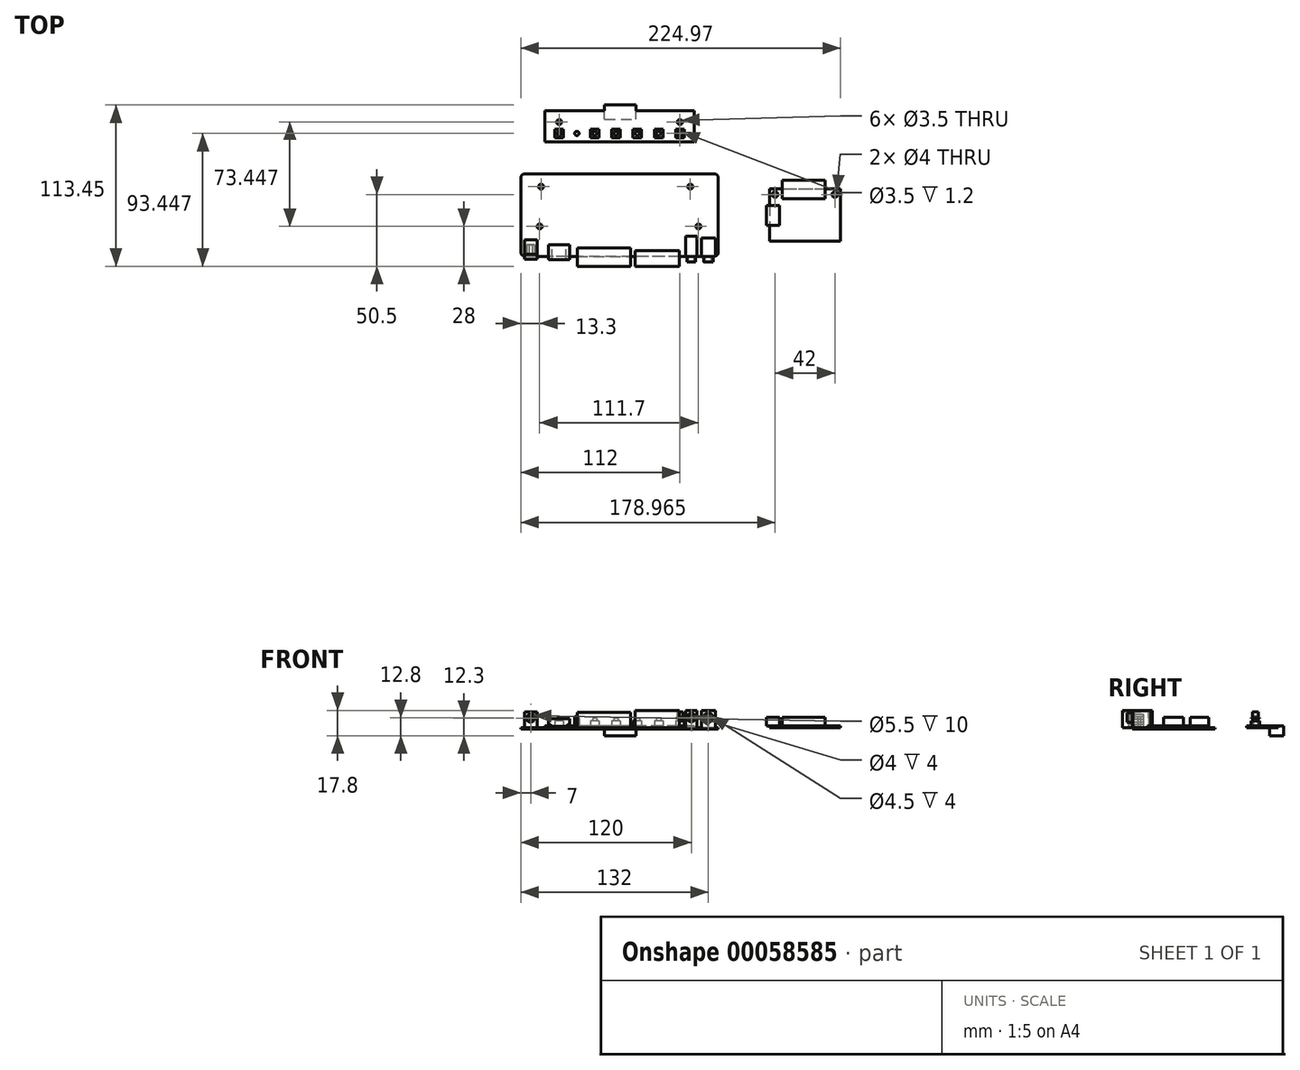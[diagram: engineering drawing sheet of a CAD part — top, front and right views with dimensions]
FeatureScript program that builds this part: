
annotation { "Feature Type Name" : "Feature", "Feature Type Description" : "" }
export const myFeature = defineFeature(function(context is Context, id is Id, definition is map)
    precondition{}
    {
        {
            var Q0;
            Q0=qCreatedBy(makeId("Top.planeOp"),FACE);
            var sketch = newSketch(context, id + "F0", { "sketchPlane" : qUnion([Q0])});
            skLineSegment(sketch, "E0.rect.bottom", {"start": v(69.5, 29) * mm, "end": v(-69.5, 29) * mm});
            skLineSegment(sketch, "E0.rect.top", {"start": v(69.5, -29) * mm, "end": v(-69.5, -29) * mm});
            skLineSegment(sketch, "E0.rect.left", {"start": v(69.5, 29) * mm, "end": v(69.5, -29) * mm});
            skLineSegment(sketch, "E0.rect.right", {"start": v(-69.5, 29) * mm, "end": v(-69.5, -29) * mm});
            skPoint(sketch, "E0.rect.middle", {"position": v(0, 0) * mm});
            skCircle(sketch, "E1", {"center": v(-56.2, -8) * mm, "radius": 1.75 * mm});
            skCircle(sketch, "E2", {"center": v(-55.2, 20) * mm, "radius": 1.75 * mm});
            skCircle(sketch, "E3", {"center": v(49.8, 20) * mm, "radius": 1.75 * mm});
            skCircle(sketch, "E4", {"center": v(55.5, -8) * mm, "radius": 1.75 * mm});
            skLineSegment(sketch, "E5", {"start": v(-77.59, -8) * mm, "end": v(188.59, -8) * mm, "construction": true});
            skLineSegment(sketch, "E6", {"start": v(-78.3, 20) * mm, "end": v(177.9, 20) * mm, "construction": true});
            skSolve(sketch);
        }
        {
            var Q0;
            Q0=qSketchRegion(id+"F0",true);
            extrude(context, id + "F1", {"entities" : qUnion([Q0]), "oppositeDirection" : true, "depth" : 1.2 * mm});
        }
        {
            var Q0;
            Q0=makeQuery(id+"F1.opExtrude","CAP_FACE",FACE,{"disambiguationData":[OSD([sQuery(id+"F0.wireOp",EDGE,"E0.rect.bottom"),sQuery(id+"F0.wireOp",EDGE,"E0.rect.top"),sQuery(id+"F0.wireOp",EDGE,"E0.rect.left"),sQuery(id+"F0.wireOp",EDGE,"E0.rect.right"),sQuery(id+"F0.wireOp",EDGE,"E1"),sQuery(id+"F0.wireOp",EDGE,"E2"),sQuery(id+"F0.wireOp",EDGE,"E3"),sQuery(id+"F0.wireOp",EDGE,"E4")])],"isStart":true});
            var sketch = newSketch(context, id + "F2", { "sketchPlane" : qUnion([Q0])});
            skLineSegment(sketch, "E7.rect.bottom", {"start": v(-58.1, -27.7) * mm, "end": v(-66.9, -27.7) * mm});
            skLineSegment(sketch, "E7.rect.top", {"start": v(-58.1, -31) * mm, "end": v(-66.9, -31) * mm});
            skLineSegment(sketch, "E7.rect.left", {"start": v(-58.1, -27.7) * mm, "end": v(-58.1, -31) * mm});
            skLineSegment(sketch, "E7.rect.right", {"start": v(-66.9, -27.7) * mm, "end": v(-66.9, -31) * mm});
            skPoint(sketch, "E7.rect.middle", {"position": v(-62.5, -29.35) * mm});
            skSolve(sketch);
        }
        {
            var Q0;
            Q0=qSketchRegion(id+"F2",true);
            extrude(context, id + "F3", {"entities" : qUnion([Q0]), "operationType" : NewBodyOperationType.ADD, "depth" : 11 * mm});
        }
        {
            var Q0;
            Q0=makeQuery(id+"F3.opExtrude","SWEPT_FACE",FACE,{"disambiguationData":[OSD([sQuery(id+"F2.wireOp",EDGE,"E7.rect.top")])]});
            var sketch = newSketch(context, id + "F4", { "sketchPlane" : qUnion([Q0])});
            skPoint(sketch, "E8.centerSnap0", {"position": v(-62.5, 11) * mm});
            skCircle(sketch, "E9", {"center": v(-62.5, 6.5) * mm, "radius": 4.4 * mm});
            skLineSegment(sketch, "E10", {"start": v(-66.9, 6.5) * mm, "end": v(-66.9, 0) * mm});
            skLineSegment(sketch, "E11", {"start": v(-66.9, 0) * mm, "end": v(-58.1, 0) * mm});
            skLineSegment(sketch, "E12", {"start": v(-58.1, 0) * mm, "end": v(-58.1, 6.5) * mm});
            skSolve(sketch);
        }
        {
            var Q0;
            Q0=qSketchRegion(id+"F4",true);
            extrude(context, id + "F5", {"entities" : qUnion([Q0]), "operationType" : NewBodyOperationType.ADD, "oppositeDirection" : true, "depth" : 13.5 * mm});
        }
        {
            var Q0;
            Q0=makeQuery(id+"F3.opExtrude","SWEPT_FACE",FACE,{"disambiguationData":[OSD([sQuery(id+"F2.wireOp",EDGE,"E7.rect.top")])]});
            var sketch = newSketch(context, id + "F6", { "sketchPlane" : qUnion([Q0])});
            skPoint(sketch, "E13.0", {"position": v(-62.5, 6.5) * mm});
            skCircle(sketch, "E14", {"center": v(-62.5, 6.5) * mm, "radius": 2.75 * mm});
            skCircle(sketch, "E15", {"center": v(-62.5, 6.5) * mm, "radius": 1.05 * mm});
            skSolve(sketch);
        }
        {
            var Q0;
            Q0=qSketchRegion(id+"F6",true);
            extrude(context, id + "F7", {"entities" : qUnion([Q0]), "operationType" : NewBodyOperationType.REMOVE, "oppositeDirection" : true, "depth" : 10 * mm});
        }
        {
            var Q0;
            Q0=makeQuery(id+"F1.opExtrude","SWEPT_FACE",FACE,{"disambiguationData":[OSD([sQuery(id+"F0.wireOp",EDGE,"E0.rect.top")])]});
            var sketch = newSketch(context, id + "F8", { "sketchPlane" : qUnion([Q0])});
            skLineSegment(sketch, "E16", {"start": v(-42.5, -5.04) * mm, "end": v(-42.5, 9.42) * mm, "construction": true});
            skLineSegment(sketch, "E17", {"start": v(-50, 2.53) * mm, "end": v(-50, 6.3) * mm});
            skLineSegment(sketch, "E18", {"start": v(-50, 6.3) * mm, "end": v(-42.5, 6.3) * mm});
            skLineSegment(sketch, "E19.MirrorCS", {"start": v(-35, 6.3) * mm, "end": v(-42.5, 6.3) * mm});
            skLineSegment(sketch, "E20.MirrorCS", {"start": v(-35, 2.53) * mm, "end": v(-35, 6.3) * mm});
            skLineSegment(sketch, "E21", {"start": v(-42.5, 0.7) * mm, "end": v(-47.5, 0.7) * mm});
            skLineSegment(sketch, "E22.MirrorCS", {"start": v(-42.5, 0.7) * mm, "end": v(-37.5, 0.7) * mm});
            skLineSegment(sketch, "E23", {"start": v(-47.5, 0.7) * mm, "end": v(-50, 2.53) * mm});
            skLineSegment(sketch, "E24", {"start": v(-37.5, 0.7) * mm, "end": v(-35, 2.53) * mm});
            skSolve(sketch);
        }
        {
            var Q0;
            Q0=qSketchRegion(id+"F8",true);
            extrude(context, id + "F9", {"entities" : qUnion([Q0]), "depth" : 2.5 * mm, "hasSecondDirection" : true, "secondDirectionOppositeDirection" : true, "secondDirectionDepth" : 8 * mm});
        }
        {
            var Q0;
            Q0=makeQuery(id+"F9.opExtrude","SWEPT_FACE",FACE,{"disambiguationData":[OSD([sQuery(id+"F8.wireOp",EDGE,"E18"),sQuery(id+"F8.wireOp",EDGE,"E19.MirrorCS")])]});
            var sketch = newSketch(context, id + "F10", { "sketchPlane" : qUnion([Q0])});
            skLineSegment(sketch, "E25.bottom", {"start": v(-50, -21) * mm, "end": v(-49.5, -21) * mm});
            skLineSegment(sketch, "E25.top", {"start": v(-50, -27) * mm, "end": v(-49.5, -27) * mm});
            skLineSegment(sketch, "E25.left", {"start": v(-50, -21) * mm, "end": v(-50, -27) * mm});
            skLineSegment(sketch, "E25.right", {"start": v(-49.5, -21) * mm, "end": v(-49.5, -27) * mm});
            skLineSegment(sketch, "E26.bottom", {"start": v(-35, -21) * mm, "end": v(-35.5, -21) * mm});
            skLineSegment(sketch, "E26.top", {"start": v(-35, -27) * mm, "end": v(-35.5, -27) * mm});
            skLineSegment(sketch, "E26.left", {"start": v(-35, -21) * mm, "end": v(-35, -27) * mm});
            skLineSegment(sketch, "E26.right", {"start": v(-35.5, -21) * mm, "end": v(-35.5, -27) * mm});
            skSolve(sketch);
        }
        {
            var Q0;
            Q0=qSketchRegion(id+"F10",true);
            var Q1;
            Q1=makeQuery(id+"F1.opExtrude","CAP_FACE",FACE,{"disambiguationData":[OSD([sQuery(id+"F0.wireOp",EDGE,"E0.rect.bottom"),sQuery(id+"F0.wireOp",EDGE,"E0.rect.top"),sQuery(id+"F0.wireOp",EDGE,"E0.rect.left"),sQuery(id+"F0.wireOp",EDGE,"E0.rect.right"),sQuery(id+"F0.wireOp",EDGE,"E1"),sQuery(id+"F0.wireOp",EDGE,"E2"),sQuery(id+"F0.wireOp",EDGE,"E3"),sQuery(id+"F0.wireOp",EDGE,"E4")])],"isStart":true});
            extrude(context, id + "F11", {"entities" : qUnion([Q0]), "operationType" : NewBodyOperationType.ADD, "endBound" : BoundingType.UP_TO_SURFACE, "oppositeDirection" : true, "endBoundEntityFace" : qUnion([Q1]), "depth" : 25 * mm});
        }
        {
            var Q0;
            Q0=makeQuery(id+"F1.opExtrude","SWEPT_FACE",FACE,{"disambiguationData":[OSD([sQuery(id+"F0.wireOp",EDGE,"E0.rect.top")])]});
            var sketch = newSketch(context, id + "F12", { "sketchPlane" : qUnion([Q0])});
            skLineSegment(sketch, "E27", {"start": v(-11, 12.94) * mm, "end": v(-11, -7.27) * mm, "construction": true});
            skLineSegment(sketch, "E28.rect.bottom", {"start": v(-29.75, 0) * mm, "end": v(7.75, 0) * mm});
            skLineSegment(sketch, "E28.rect.top", {"start": v(-29.75, 10.8) * mm, "end": v(7.75, 10.8) * mm});
            skLineSegment(sketch, "E28.rect.left", {"start": v(-29.75, 0) * mm, "end": v(-29.75, 10.8) * mm});
            skLineSegment(sketch, "E28.rect.right", {"start": v(7.75, 0) * mm, "end": v(7.75, 10.8) * mm});
            skPoint(sketch, "E28.rect.middle", {"position": v(-11, 5.4) * mm});
            skSolve(sketch);
        }
        {
            var Q0;
            Q0=makeQuery(id+"F12.imprint","IMPRINT",FACE,{"disambiguationData":[TD([[makeQuery(id+"F12.imprint","IMPRINT",EDGE,{"derivedFrom":sQuery(id+"F12.wireOp",EDGE,"E28.rect.bottom")}),-1.0]])]});
            extrude(context, id + "F13", {"entities" : qUnion([Q0]), "operationType" : NewBodyOperationType.ADD, "oppositeDirection" : true, "depth" : 6 * mm});
        }
        {
            var Q0;
            Q0=makeQuery(id+"F13.boolean.opBoolean","MERGE",FACE,{"derivedFrom":[makeQuery(id+"F1.opExtrude","SWEPT_FACE",FACE,{"disambiguationData":[OSD([sQuery(id+"F0.wireOp",EDGE,"E0.rect.top")])]}),makeQuery(id+"F13.opExtrude","CAP_FACE",FACE,{"disambiguationData":[OSD([sQuery(id+"F12.wireOp",EDGE,"E28.rect.bottom"),sQuery(id+"F12.wireOp",EDGE,"E28.rect.top"),sQuery(id+"F12.wireOp",EDGE,"E28.rect.left"),sQuery(id+"F12.wireOp",EDGE,"E28.rect.right")])],"isStart":true})]});
            var sketch = newSketch(context, id + "F14", { "sketchPlane" : qUnion([Q0])});
            skLineSegment(sketch, "E29.0", {"start": v(-11, 12.94) * mm, "end": v(-11, -7.27) * mm, "construction": true});
            skLineSegment(sketch, "E30", {"start": v(-11, 8.9) * mm, "end": v(-23, 8.9) * mm});
            skLineSegment(sketch, "E31", {"start": v(-23, 8.9) * mm, "end": v(-23, 4.3) * mm});
            skLineSegment(sketch, "E32", {"start": v(-23, 4.3) * mm, "end": v(-22, 1.1) * mm});
            skLineSegment(sketch, "E33", {"start": v(-22, 1.1) * mm, "end": v(-11, 1.1) * mm});
            skPoint(sketch, "E33.endSnap0", {"position": v(-11, 2.83) * mm});
            skLineSegment(sketch, "E34.MirrorCS", {"start": v(-11, 8.9) * mm, "end": v(1, 8.9) * mm});
            skLineSegment(sketch, "E35.MirrorCS", {"start": v(1, 8.9) * mm, "end": v(1, 4.3) * mm});
            skLineSegment(sketch, "E36.MirrorCS", {"start": v(1, 4.3) * mm, "end": v(0, 1.1) * mm});
            skLineSegment(sketch, "E37.MirrorCS", {"start": v(0, 1.1) * mm, "end": v(-11, 1.1) * mm});
            skLineSegment(sketch, "E38", {"start": v(-33.58, 5) * mm, "end": v(6.6, 5) * mm, "construction": true});
            skCircle(sketch, "E39", {"center": v(-27.25, 5) * mm, "radius": 1.25 * mm});
            skCircle(sketch, "E40.cCircle", {"center": v(-27.25, 5) * mm, "radius": 2.4 * mm, "construction": true});
            skLineSegment(sketch, "E40.0", {"start": v(-24.85, 6.39) * mm, "end": v(-24.85, 3.61) * mm});
            skLineSegment(sketch, "E40.1", {"start": v(-24.85, 3.61) * mm, "end": v(-27.25, 2.23) * mm});
            skLineSegment(sketch, "E40.2", {"start": v(-27.25, 2.23) * mm, "end": v(-29.65, 3.61) * mm});
            skLineSegment(sketch, "E40.3", {"start": v(-29.65, 3.61) * mm, "end": v(-29.65, 6.39) * mm});
            skLineSegment(sketch, "E40.4", {"start": v(-29.65, 6.39) * mm, "end": v(-27.25, 7.77) * mm});
            skLineSegment(sketch, "E40.5", {"start": v(-27.25, 7.77) * mm, "end": v(-24.85, 6.39) * mm});
            skPoint(sketch, "E40.0.midPoint", {"position": v(-24.85, 5) * mm});
            skLineSegment(sketch, "E41.MirrorCS", {"start": v(2.85, 6.39) * mm, "end": v(2.85, 3.61) * mm});
            skLineSegment(sketch, "E42.MirrorCS", {"start": v(5.25, 7.77) * mm, "end": v(2.85, 6.39) * mm});
            skLineSegment(sketch, "E43.MirrorCS", {"start": v(7.65, 6.39) * mm, "end": v(5.25, 7.77) * mm});
            skLineSegment(sketch, "E44.MirrorCS", {"start": v(7.65, 3.61) * mm, "end": v(7.65, 6.39) * mm});
            skLineSegment(sketch, "E45.MirrorCS", {"start": v(5.25, 2.23) * mm, "end": v(7.65, 3.61) * mm});
            skLineSegment(sketch, "E46.MirrorCS", {"start": v(2.85, 3.61) * mm, "end": v(5.25, 2.23) * mm});
            skCircle(sketch, "E47.MirrorC", {"center": v(5.25, 5) * mm, "radius": 1.25 * mm});
            skSolve(sketch);
        }
        {
            var Q0;
            Q0=qSketchRegion(id+"F14",true);
            extrude(context, id + "F15", {"entities" : qUnion([Q0]), "operationType" : NewBodyOperationType.ADD, "depth" : 7 * mm});
        }
        {
            var Q0;
            {var subQ6=sQuery(id+"F0.wireOp",EDGE,"E0.rect.left");var subQ7=sQuery(id+"F0.wireOp",EDGE,"E0.rect.top");var subQ9=sQuery(id+"F12.wireOp",EDGE,"E28.rect.right");var subQ10=sQuery(id+"F12.wireOp",EDGE,"E28.rect.left");var subQ12=sQuery(id+"F12.wireOp",EDGE,"E28.rect.top");Q0=makeQuery(id+"F15.boolean.opBoolean","SPLIT",FACE,{"disambiguationData":[TD([makeQuery(id+"F1.opExtrude","SWEPT_FACE",FACE,{"disambiguationData":[OSD([subQ6])]})])],"derivedFrom":makeQuery(id+"F13.boolean.opBoolean","MERGE",FACE,{"derivedFrom":[makeQuery(id+"F1.opExtrude","SWEPT_FACE",FACE,{"disambiguationData":[OSD([subQ7])]}),makeQuery(id+"F13.opExtrude","CAP_FACE",FACE,{"disambiguationData":[OSD([sQuery(id+"F12.wireOp",EDGE,"E28.rect.bottom"),subQ12,subQ10,subQ9])],"isStart":true})]})});}
            var sketch = newSketch(context, id + "F16", { "sketchPlane" : qUnion([Q0])});
            skLineSegment(sketch, "E48", {"start": v(26.5, 12.4) * mm, "end": v(26.5, -10.3) * mm, "construction": true});
            skLineSegment(sketch, "E49.rect.bottom", {"start": v(11, 0) * mm, "end": v(42, 0) * mm});
            skLineSegment(sketch, "E49.rect.top", {"start": v(11, 12) * mm, "end": v(42, 12) * mm});
            skLineSegment(sketch, "E49.rect.left", {"start": v(11, 0) * mm, "end": v(11, 12) * mm});
            skLineSegment(sketch, "E49.rect.right", {"start": v(42, 0) * mm, "end": v(42, 12) * mm});
            skPoint(sketch, "E49.rect.middle", {"position": v(26.5, 6) * mm});
            skSolve(sketch);
        }
        {
            var Q0;
            Q0=qSketchRegion(id+"F16",true);
            extrude(context, id + "F17", {"entities" : qUnion([Q0]), "operationType" : NewBodyOperationType.ADD, "oppositeDirection" : true, "depth" : 4 * mm});
        }
        {
            var Q0;
            {var subQ6=sQuery(id+"F0.wireOp",EDGE,"E0.rect.left");var subQ7=sQuery(id+"F0.wireOp",EDGE,"E0.rect.top");var subQ9=sQuery(id+"F12.wireOp",EDGE,"E28.rect.right");var subQ10=sQuery(id+"F12.wireOp",EDGE,"E28.rect.left");var subQ12=sQuery(id+"F12.wireOp",EDGE,"E28.rect.top");Q0=makeQuery(id+"F17.boolean.opBoolean","MERGE",FACE,{"derivedFrom":[makeQuery(id+"F15.boolean.opBoolean","SPLIT",FACE,{"disambiguationData":[TD([makeQuery(id+"F1.opExtrude","SWEPT_FACE",FACE,{"disambiguationData":[OSD([subQ6])]})])],"derivedFrom":makeQuery(id+"F13.boolean.opBoolean","MERGE",FACE,{"derivedFrom":[makeQuery(id+"F1.opExtrude","SWEPT_FACE",FACE,{"disambiguationData":[OSD([subQ7])]}),makeQuery(id+"F13.opExtrude","CAP_FACE",FACE,{"disambiguationData":[OSD([sQuery(id+"F12.wireOp",EDGE,"E28.rect.bottom"),subQ12,subQ10,subQ9])],"isStart":true})]})}),makeQuery(id+"F17.opExtrude","CAP_FACE",FACE,{"disambiguationData":[OSD([sQuery(id+"F16.wireOp",EDGE,"E49.rect.bottom"),sQuery(id+"F16.wireOp",EDGE,"E49.rect.top"),sQuery(id+"F16.wireOp",EDGE,"E49.rect.left"),sQuery(id+"F16.wireOp",EDGE,"E49.rect.right")])],"isStart":true})]});}
            var sketch = newSketch(context, id + "F18", { "sketchPlane" : qUnion([Q0])});
            skLineSegment(sketch, "E50.0", {"start": v(26.5, 12.4) * mm, "end": v(26.5, -10.3) * mm, "construction": true});
            skLineSegment(sketch, "E51", {"start": v(10.25, 5) * mm, "end": v(41.25, 5) * mm, "construction": true});
            skLineSegment(sketch, "E52", {"start": v(26.5, 8.9) * mm, "end": v(18.35, 8.9) * mm});
            skLineSegment(sketch, "E53", {"start": v(18.35, 8.9) * mm, "end": v(19.85, 1.1) * mm});
            skLineSegment(sketch, "E54", {"start": v(19.85, 1.1) * mm, "end": v(26.5, 1.1) * mm});
            skLineSegment(sketch, "E55.MirrorCS", {"start": v(26.5, 8.9) * mm, "end": v(34.65, 8.9) * mm});
            skLineSegment(sketch, "E56.MirrorCS", {"start": v(33.15, 1.1) * mm, "end": v(26.5, 1.1) * mm});
            skLineSegment(sketch, "E57.MirrorCS", {"start": v(34.65, 8.9) * mm, "end": v(33.15, 1.1) * mm});
            skLineSegment(sketch, "E58", {"start": v(9.44, 6.3) * mm, "end": v(48.02, 6.3) * mm, "construction": true});
            skCircle(sketch, "E59.cCircle", {"center": v(14, 6.3) * mm, "radius": 2 * mm, "construction": true});
            skLineSegment(sketch, "E59.0", {"start": v(16, 7.45) * mm, "end": v(16, 5.15) * mm});
            skLineSegment(sketch, "E59.1", {"start": v(16, 5.15) * mm, "end": v(14, 4) * mm});
            skLineSegment(sketch, "E59.2", {"start": v(14, 4) * mm, "end": v(12, 5.15) * mm});
            skLineSegment(sketch, "E59.3", {"start": v(12, 5.15) * mm, "end": v(12, 7.45) * mm});
            skLineSegment(sketch, "E59.4", {"start": v(12, 7.45) * mm, "end": v(14, 8.6) * mm});
            skLineSegment(sketch, "E59.5", {"start": v(14, 8.6) * mm, "end": v(16, 7.45) * mm});
            skPoint(sketch, "E59.0.midPoint", {"position": v(16, 6.3) * mm});
            skCircle(sketch, "E60", {"center": v(14, 6.3) * mm, "radius": 1 * mm});
            skLineSegment(sketch, "E61.MirrorCS", {"start": v(39, 8.6) * mm, "end": v(37, 7.45) * mm});
            skLineSegment(sketch, "E62.MirrorCS", {"start": v(37, 7.45) * mm, "end": v(37, 5.15) * mm});
            skLineSegment(sketch, "E63.MirrorCS", {"start": v(37, 5.15) * mm, "end": v(39, 4) * mm});
            skLineSegment(sketch, "E64.MirrorCS", {"start": v(39, 4) * mm, "end": v(41, 5.15) * mm});
            skLineSegment(sketch, "E65.MirrorCS", {"start": v(41, 5.15) * mm, "end": v(41, 7.45) * mm});
            skLineSegment(sketch, "E66.MirrorCS", {"start": v(41, 7.45) * mm, "end": v(39, 8.6) * mm});
            skCircle(sketch, "E67.MirrorC", {"center": v(39, 6.3) * mm, "radius": 1 * mm});
            skSolve(sketch);
        }
        {
            var Q0;
            Q0=qSketchRegion(id+"F18",true);
            extrude(context, id + "F19", {"entities" : qUnion([Q0]), "operationType" : NewBodyOperationType.ADD, "depth" : 6 * mm});
        }
        {
            var Q0;
            Q0=makeQuery(id+"F1.opExtrude","CAP_FACE",FACE,{"disambiguationData":[OSD([sQuery(id+"F0.wireOp",EDGE,"E0.rect.bottom"),sQuery(id+"F0.wireOp",EDGE,"E0.rect.top"),sQuery(id+"F0.wireOp",EDGE,"E0.rect.left"),sQuery(id+"F0.wireOp",EDGE,"E0.rect.right"),sQuery(id+"F0.wireOp",EDGE,"E1"),sQuery(id+"F0.wireOp",EDGE,"E2"),sQuery(id+"F0.wireOp",EDGE,"E3"),sQuery(id+"F0.wireOp",EDGE,"E4")])],"isStart":true});
            var sketch = newSketch(context, id + "F20", { "sketchPlane" : qUnion([Q0])});
            skLineSegment(sketch, "E68.rect.bottom", {"start": v(54.5, -29) * mm, "end": v(46.5, -29) * mm});
            skLineSegment(sketch, "E68.rect.top", {"start": v(54.5, -15) * mm, "end": v(46.5, -15) * mm});
            skLineSegment(sketch, "E68.rect.left", {"start": v(54.5, -29) * mm, "end": v(54.5, -15) * mm});
            skLineSegment(sketch, "E68.rect.right", {"start": v(46.5, -29) * mm, "end": v(46.5, -15) * mm});
            skPoint(sketch, "E68.rect.middle", {"position": v(50.5, -22) * mm});
            skLineSegment(sketch, "E69.rect.bottom", {"start": v(67.5, -29) * mm, "end": v(57.5, -29) * mm});
            skLineSegment(sketch, "E69.rect.top", {"start": v(67.5, -16) * mm, "end": v(57.5, -16) * mm});
            skLineSegment(sketch, "E69.rect.left", {"start": v(67.5, -29) * mm, "end": v(67.5, -16) * mm});
            skLineSegment(sketch, "E69.rect.right", {"start": v(57.5, -29) * mm, "end": v(57.5, -16) * mm});
            skPoint(sketch, "E69.rect.middle", {"position": v(62.5, -22.5) * mm});
            skSolve(sketch);
        }
        {
            var Q0;
            Q0=qSketchRegion(id+"F20",true);
            extrude(context, id + "F21", {"entities" : qUnion([Q0]), "operationType" : NewBodyOperationType.ADD, "depth" : 12 * mm});
        }
        {
            var Q0;
            {var subQ5=sQuery(id+"F0.wireOp",EDGE,"E0.rect.left");var subQ6=sQuery(id+"F0.wireOp",EDGE,"E0.rect.top");var subQ9=sQuery(id+"F12.wireOp",EDGE,"E28.rect.top");var subQ11=sQuery(id+"F16.wireOp",EDGE,"E49.rect.left");var subQ12=sQuery(id+"F16.wireOp",EDGE,"E49.rect.right");var subQ13=sQuery(id+"F16.wireOp",EDGE,"E49.rect.top");var subQ24=makeQuery(id+"F1.opExtrude","SWEPT_FACE",FACE,{"disambiguationData":[OSD([subQ5])]});var subQ33=sQuery(id+"F12.wireOp",EDGE,"E28.rect.left");var subQ35=sQuery(id+"F12.wireOp",EDGE,"E28.rect.right");Q0=makeQuery(id+"F21.boolean.opBoolean","MERGE",FACE,{"derivedFrom":[makeQuery(id+"F19.boolean.opBoolean","SPLIT",FACE,{"disambiguationData":[TD([subQ24])],"derivedFrom":makeQuery(id+"F17.boolean.opBoolean","MERGE",FACE,{"derivedFrom":[makeQuery(id+"F15.boolean.opBoolean","SPLIT",FACE,{"disambiguationData":[TD([subQ24])],"derivedFrom":makeQuery(id+"F13.boolean.opBoolean","MERGE",FACE,{"derivedFrom":[makeQuery(id+"F1.opExtrude","SWEPT_FACE",FACE,{"disambiguationData":[OSD([subQ6])]}),makeQuery(id+"F13.opExtrude","CAP_FACE",FACE,{"disambiguationData":[OSD([sQuery(id+"F12.wireOp",EDGE,"E28.rect.bottom"),subQ9,subQ33,subQ35])],"isStart":true})]})}),makeQuery(id+"F17.opExtrude","CAP_FACE",FACE,{"disambiguationData":[OSD([sQuery(id+"F16.wireOp",EDGE,"E49.rect.bottom"),subQ13,subQ11,subQ12])],"isStart":true})]})}),makeQuery(id+"F21.opExtrude","SWEPT_FACE",FACE,{"disambiguationData":[OSD([sQuery(id+"F20.wireOp",EDGE,"E68.rect.bottom")])]}),makeQuery(id+"F21.opExtrude","SWEPT_FACE",FACE,{"disambiguationData":[OSD([sQuery(id+"F20.wireOp",EDGE,"E69.rect.bottom")])]})]});}
            var sketch = newSketch(context, id + "F22", { "sketchPlane" : qUnion([Q0])});
            skCircle(sketch, "E70", {"center": v(50.5, 7) * mm, "radius": 3 * mm});
            skCircle(sketch, "E71", {"center": v(62.5, 7) * mm, "radius": 3.25 * mm});
            skPoint(sketch, "E71.centerSnap0", {"position": v(62.5, 12) * mm});
            skCircle(sketch, "E72.0", {"center": v(50.5, 7) * mm, "radius": 2 * mm});
            skCircle(sketch, "E73.0", {"center": v(62.5, 7) * mm, "radius": 2.25 * mm});
            skSolve(sketch);
        }
        {
            var Q0;
            Q0=qSketchRegion(id+"F22",true);
            extrude(context, id + "F23", {"entities" : qUnion([Q0]), "operationType" : NewBodyOperationType.ADD, "depth" : 4 * mm});
        }
        {
            var Q0;
            Q0=makeQuery(id+"F1.opExtrude","SWEPT_EDGE",EDGE,{"disambiguationData":[OSD([sQuery(id+"F0.wireOp",EDGE,"E0.rect.top"),sQuery(id+"F0.wireOp",EDGE,"E0.rect.left")])]});
            var Q1;
            Q1=makeQuery(id+"F1.opExtrude","SWEPT_EDGE",EDGE,{"disambiguationData":[OSD([sQuery(id+"F0.wireOp",EDGE,"E0.rect.bottom"),sQuery(id+"F0.wireOp",EDGE,"E0.rect.left")])]});
            var Q2;
            Q2=makeQuery(id+"F1.opExtrude","SWEPT_EDGE",EDGE,{"disambiguationData":[OSD([sQuery(id+"F0.wireOp",EDGE,"E0.rect.top"),sQuery(id+"F0.wireOp",EDGE,"E0.rect.right")])]});
            var Q3;
            Q3=makeQuery(id+"F1.opExtrude","SWEPT_EDGE",EDGE,{"disambiguationData":[OSD([sQuery(id+"F0.wireOp",EDGE,"E0.rect.bottom"),sQuery(id+"F0.wireOp",EDGE,"E0.rect.right")])]});
            fillet(context, id + "F24", {"entities" : qUnion([Q0, Q1, Q2, Q3]), "radius" : 3 * mm, "tangentPropagation" : true, "allowEdgeOverflow" : false});
        }
        {
            var Q0;
            Q0=qCreatedBy(makeId("Top.planeOp"),FACE);
            var sketch = newSketch(context, id + "F25", { "sketchPlane" : qUnion([Q0])});
            skLineSegment(sketch, "E74", {"start": v(86.39, 0) * mm, "end": v(166.5, 0) * mm, "construction": true});
            skLineSegment(sketch, "E75", {"start": v(130.47, 33.3) * mm, "end": v(130.47, -40.38) * mm, "construction": true});
            skLineSegment(sketch, "E76.rect.bottom", {"start": v(105.47, 18.5) * mm, "end": v(155.47, 18.5) * mm});
            skLineSegment(sketch, "E76.rect.top", {"start": v(105.47, -18.5) * mm, "end": v(155.47, -18.5) * mm});
            skLineSegment(sketch, "E76.rect.left", {"start": v(105.47, 18.5) * mm, "end": v(105.47, -18.5) * mm});
            skLineSegment(sketch, "E76.rect.right", {"start": v(155.47, 18.5) * mm, "end": v(155.47, -18.5) * mm});
            skPoint(sketch, "E76.rect.middle", {"position": v(130.47, 0) * mm});
            skCircle(sketch, "E77", {"center": v(109.47, 14.5) * mm, "radius": 2 * mm});
            skCircle(sketch, "E78", {"center": v(151.47, 14.5) * mm, "radius": 2 * mm});
            skSolve(sketch);
        }
        {
            var Q0;
            Q0=qSketchRegion(id+"F25",true);
            extrude(context, id + "F26", {"entities" : qUnion([Q0]), "depth" : 1.2 * mm});
        }
        {
            var Q0;
            Q0=makeQuery(id+"F26.opExtrude","CAP_FACE",FACE,{"disambiguationData":[OSD([sQuery(id+"F25.wireOp",EDGE,"E76.rect.bottom"),sQuery(id+"F25.wireOp",EDGE,"E76.rect.top"),sQuery(id+"F25.wireOp",EDGE,"E76.rect.left"),sQuery(id+"F25.wireOp",EDGE,"E76.rect.right"),sQuery(id+"F25.wireOp",EDGE,"E77"),sQuery(id+"F25.wireOp",EDGE,"E78")])],"isStart":false});
            var sketch = newSketch(context, id + "F27", { "sketchPlane" : qUnion([Q0])});
            skLineSegment(sketch, "E79.bottom", {"start": v(114.47, 24.5) * mm, "end": v(144.47, 24.5) * mm});
            skLineSegment(sketch, "E79.top", {"start": v(114.47, 11.5) * mm, "end": v(144.47, 11.5) * mm});
            skLineSegment(sketch, "E79.left", {"start": v(114.47, 24.5) * mm, "end": v(114.47, 11.5) * mm});
            skLineSegment(sketch, "E79.right", {"start": v(144.47, 24.5) * mm, "end": v(144.47, 11.5) * mm});
            skLineSegment(sketch, "E80.bottom", {"start": v(103.47, 6.77) * mm, "end": v(112.47, 6.77) * mm});
            skLineSegment(sketch, "E80.top", {"start": v(103.47, -7.23) * mm, "end": v(112.47, -7.23) * mm});
            skLineSegment(sketch, "E80.left", {"start": v(103.47, 6.77) * mm, "end": v(103.47, -7.23) * mm});
            skLineSegment(sketch, "E80.right", {"start": v(112.47, 6.77) * mm, "end": v(112.47, -7.23) * mm});
            skSolve(sketch);
        }
        {
            var Q0;
            Q0=qSketchRegion(id+"F27",true);
            extrude(context, id + "F28", {"entities" : qUnion([Q0]), "operationType" : NewBodyOperationType.ADD, "depth" : 6 * mm});
        }
        {
            var Q0;
            Q0=qCreatedBy(makeId("Top.planeOp"),FACE);
            var sketch = newSketch(context, id + "F29", { "sketchPlane" : qUnion([Q0])});
            skLineSegment(sketch, "E81.rect.bottom", {"start": v(52.5, 51.45) * mm, "end": v(-52.5, 51.45) * mm});
            skLineSegment(sketch, "E81.rect.top", {"start": v(52.5, 73.45) * mm, "end": v(-52.5, 73.45) * mm});
            skLineSegment(sketch, "E81.rect.left", {"start": v(52.5, 51.45) * mm, "end": v(52.5, 73.45) * mm});
            skLineSegment(sketch, "E81.rect.right", {"start": v(-52.5, 51.45) * mm, "end": v(-52.5, 73.45) * mm});
            skPoint(sketch, "E81.rect.middle", {"position": v(0, 62.45) * mm});
            skCircle(sketch, "E82", {"center": v(-42.5, 65.45) * mm, "radius": 1.75 * mm});
            skCircle(sketch, "E83", {"center": v(42.5, 65.45) * mm, "radius": 1.75 * mm});
            skSolve(sketch);
        }
        {
            var Q0;
            Q0=qSketchRegion(id+"F29",true);
            extrude(context, id + "F30", {"entities" : qUnion([Q0]), "depth" : 1.2 * mm});
        }
        {
            var Q0;
            Q0=makeQuery(id+"F30.opExtrude","CAP_FACE",FACE,{"disambiguationData":[OSD([sQuery(id+"F29.wireOp",EDGE,"E81.rect.bottom"),sQuery(id+"F29.wireOp",EDGE,"E81.rect.top"),sQuery(id+"F29.wireOp",EDGE,"E81.rect.left"),sQuery(id+"F29.wireOp",EDGE,"E81.rect.right"),sQuery(id+"F29.wireOp",EDGE,"E82"),sQuery(id+"F29.wireOp",EDGE,"E83")])],"isStart":false});
            var sketch = newSketch(context, id + "F31", { "sketchPlane" : qUnion([Q0])});
            skLineSegment(sketch, "E84.bottom", {"start": v(-10.5, 67.45) * mm, "end": v(11.5, 67.45) * mm});
            skLineSegment(sketch, "E84.top", {"start": v(-10.5, 77.45) * mm, "end": v(11.5, 77.45) * mm});
            skLineSegment(sketch, "E84.left", {"start": v(-10.5, 67.45) * mm, "end": v(-10.5, 77.45) * mm});
            skLineSegment(sketch, "E84.right", {"start": v(11.5, 67.45) * mm, "end": v(11.5, 77.45) * mm});
            skSolve(sketch);
        }
        {
            var Q0;
            Q0=qSketchRegion(id+"F31",true);
            extrude(context, id + "F32", {"entities" : qUnion([Q0]), "operationType" : NewBodyOperationType.ADD, "oppositeDirection" : true, "depth" : 7 * mm});
        }
        {
            var Q0;
            Q0=makeQuery(id+"F30.opExtrude","CAP_FACE",FACE,{"disambiguationData":[OSD([sQuery(id+"F29.wireOp",EDGE,"E81.rect.bottom"),sQuery(id+"F29.wireOp",EDGE,"E81.rect.top"),sQuery(id+"F29.wireOp",EDGE,"E81.rect.left"),sQuery(id+"F29.wireOp",EDGE,"E81.rect.right"),sQuery(id+"F29.wireOp",EDGE,"E82"),sQuery(id+"F29.wireOp",EDGE,"E83")])],"isStart":false});
            var sketch = newSketch(context, id + "F33", { "sketchPlane" : qUnion([Q0])});
            skLineSegment(sketch, "E85", {"start": v(-61.88, 57.45) * mm, "end": v(63.54, 57.45) * mm, "construction": true});
            skLineSegment(sketch, "E86.rect.bottom", {"start": v(-39.5, 60.45) * mm, "end": v(-45.5, 60.45) * mm});
            skLineSegment(sketch, "E86.rect.top", {"start": v(-39.5, 54.45) * mm, "end": v(-45.5, 54.45) * mm});
            skLineSegment(sketch, "E86.rect.left", {"start": v(-39.5, 60.45) * mm, "end": v(-39.5, 54.45) * mm});
            skLineSegment(sketch, "E86.rect.right", {"start": v(-45.5, 60.45) * mm, "end": v(-45.5, 54.45) * mm});
            skPoint(sketch, "E86.rect.middle", {"position": v(-42.5, 57.45) * mm});
            skPoint(sketch, "E87", {"position": v(-17.5, 57.45) * mm});
            skPoint(sketch, "E88", {"position": v(-2.5, 57.45) * mm});
            skPoint(sketch, "E89", {"position": v(12.5, 57.45) * mm});
            skPoint(sketch, "E90", {"position": v(27.5, 57.45) * mm});
            skPoint(sketch, "E91", {"position": v(42.5, 57.45) * mm});
            skLineSegment(sketch, "E92.rect.right", {"start": v(-20.5, 60.45) * mm, "end": v(-20.5, 54.45) * mm});
            skLineSegment(sketch, "E92.rect.bottom", {"start": v(-14.5, 60.45) * mm, "end": v(-20.5, 60.45) * mm});
            skLineSegment(sketch, "E92.rect.left", {"start": v(-14.5, 60.45) * mm, "end": v(-14.5, 54.45) * mm});
            skLineSegment(sketch, "E92.rect.top", {"start": v(-14.5, 54.45) * mm, "end": v(-20.5, 54.45) * mm});
            skLineSegment(sketch, "E93.1.0.0", {"start": v(0.5, 60.45) * mm, "end": v(-5.5, 60.45) * mm});
            skLineSegment(sketch, "E93.1.0.1", {"start": v(0.5, 60.45) * mm, "end": v(0.5, 54.45) * mm});
            skLineSegment(sketch, "E93.1.0.2", {"start": v(-5.5, 60.45) * mm, "end": v(-5.5, 54.45) * mm});
            skLineSegment(sketch, "E93.1.0.4", {"start": v(0.5, 54.45) * mm, "end": v(-5.5, 54.45) * mm});
            skLineSegment(sketch, "E93.2.0.0", {"start": v(15.5, 60.45) * mm, "end": v(9.5, 60.45) * mm});
            skLineSegment(sketch, "E93.2.0.1", {"start": v(15.5, 60.45) * mm, "end": v(15.5, 54.45) * mm});
            skLineSegment(sketch, "E93.2.0.2", {"start": v(9.5, 60.45) * mm, "end": v(9.5, 54.45) * mm});
            skLineSegment(sketch, "E93.2.0.4", {"start": v(15.5, 54.45) * mm, "end": v(9.5, 54.45) * mm});
            skLineSegment(sketch, "E93.3.0.0", {"start": v(30.5, 60.45) * mm, "end": v(24.5, 60.45) * mm});
            skLineSegment(sketch, "E93.3.0.1", {"start": v(30.5, 60.45) * mm, "end": v(30.5, 54.45) * mm});
            skLineSegment(sketch, "E93.3.0.2", {"start": v(24.5, 60.45) * mm, "end": v(24.5, 54.45) * mm});
            skLineSegment(sketch, "E93.3.0.4", {"start": v(30.5, 54.45) * mm, "end": v(24.5, 54.45) * mm});
            skLineSegment(sketch, "E93.4.0.0", {"start": v(45.5, 60.45) * mm, "end": v(39.5, 60.45) * mm});
            skLineSegment(sketch, "E93.4.0.1", {"start": v(45.5, 60.45) * mm, "end": v(45.5, 54.45) * mm});
            skLineSegment(sketch, "E93.4.0.2", {"start": v(39.5, 60.45) * mm, "end": v(39.5, 54.45) * mm});
            skLineSegment(sketch, "E93.4.0.4", {"start": v(45.5, 54.45) * mm, "end": v(39.5, 54.45) * mm});
            skSolve(sketch);
        }
        {
            var Q0;
            Q0=qSketchRegion(id+"F33",true);
            extrude(context, id + "F34", {"entities" : qUnion([Q0]), "operationType" : NewBodyOperationType.ADD, "depth" : 3.5 * mm});
        }
        {
            var Q0;
            Q0=makeQuery(id+"F34.opExtrude","CAP_FACE",FACE,{"disambiguationData":[OSD([sQuery(id+"F33.wireOp",EDGE,"E86.rect.bottom"),sQuery(id+"F33.wireOp",EDGE,"E86.rect.top"),sQuery(id+"F33.wireOp",EDGE,"E86.rect.left"),sQuery(id+"F33.wireOp",EDGE,"E86.rect.right")])],"isStart":false});
            var sketch = newSketch(context, id + "F35", { "sketchPlane" : qUnion([Q0])});
            skCircle(sketch, "E94", {"center": v(-42.5, 57.45) * mm, "radius": 1.5 * mm});
            skPoint(sketch, "E94.centerSnap0", {"position": v(-45.5, 57.45) * mm});
            skPoint(sketch, "E94.centerSnap1", {"position": v(-42.5, 60.45) * mm});
            skLineSegment(sketch, "E95.0", {"start": v(-20.5, 60.45) * mm, "end": v(-20.5, 54.45) * mm, "construction": true});
            skLineSegment(sketch, "E96.0", {"start": v(-14.5, 60.45) * mm, "end": v(-20.5, 60.45) * mm, "construction": true});
            skCircle(sketch, "E97", {"center": v(-17.5, 57.45) * mm, "radius": 1.5 * mm});
            skPoint(sketch, "E97.centerSnap0", {"position": v(-17.5, 60.45) * mm});
            skPoint(sketch, "E97.centerSnap1", {"position": v(-20.5, 57.45) * mm});
            skCircle(sketch, "E98.1.0.0", {"center": v(-2.5, 57.45) * mm, "radius": 1.5 * mm});
            skCircle(sketch, "E98.2.0.0", {"center": v(12.5, 57.45) * mm, "radius": 1.5 * mm});
            skCircle(sketch, "E98.3.0.0", {"center": v(27.5, 57.45) * mm, "radius": 1.5 * mm});
            skCircle(sketch, "E98.4.0.0", {"center": v(42.5, 57.45) * mm, "radius": 1.5 * mm});
            skLineSegment(sketch, "E98.direction1", {"start": v(-17.5, 57.45) * mm, "end": v(-2.5, 57.45) * mm, "construction": true});
            skSolve(sketch);
        }
        {
            var Q0;
            Q0=makeQuery(id+"F35.imprint","IMPRINT",FACE,{"disambiguationData":[TD([[makeQuery(id+"F35.imprint","IMPRINT",EDGE,{"derivedFrom":sQuery(id+"F35.wireOp",EDGE,"E94")}),1.0]])]});
            var Q1;
            Q1=makeQuery(id+"F35.imprint","IMPRINT",FACE,{"disambiguationData":[TD([[makeQuery(id+"F35.imprint","IMPRINT",EDGE,{"derivedFrom":sQuery(id+"F35.wireOp",EDGE,"E97")}),1.0]])]});
            var Q2;
            Q2=makeQuery(id+"F35.imprint","IMPRINT",FACE,{"disambiguationData":[TD([[makeQuery(id+"F35.imprint","IMPRINT",EDGE,{"derivedFrom":sQuery(id+"F35.wireOp",EDGE,"E98.1.0.0")}),1.0]])]});
            var Q3;
            Q3=makeQuery(id+"F35.imprint","IMPRINT",FACE,{"disambiguationData":[TD([[makeQuery(id+"F35.imprint","IMPRINT",EDGE,{"derivedFrom":sQuery(id+"F35.wireOp",EDGE,"E98.2.0.0")}),1.0]])]});
            var Q4;
            Q4=makeQuery(id+"F35.imprint","IMPRINT",FACE,{"disambiguationData":[TD([[makeQuery(id+"F35.imprint","IMPRINT",EDGE,{"derivedFrom":sQuery(id+"F35.wireOp",EDGE,"E98.3.0.0")}),1.0]])]});
            var Q5;
            Q5=makeQuery(id+"F35.imprint","IMPRINT",FACE,{"disambiguationData":[TD([[makeQuery(id+"F35.imprint","IMPRINT",EDGE,{"derivedFrom":sQuery(id+"F35.wireOp",EDGE,"E98.4.0.0")}),1.0]])]});
            extrude(context, id + "F36", {"entities" : qUnion([Q0, Q1, Q2, Q3, Q4, Q5]), "operationType" : NewBodyOperationType.ADD, "depth" : 2 * mm});
        }
        {
            var Q0;
            Q0=makeQuery(id+"F30.opExtrude","CAP_FACE",FACE,{"disambiguationData":[OSD([sQuery(id+"F29.wireOp",EDGE,"E81.rect.bottom"),sQuery(id+"F29.wireOp",EDGE,"E81.rect.top"),sQuery(id+"F29.wireOp",EDGE,"E81.rect.left"),sQuery(id+"F29.wireOp",EDGE,"E81.rect.right"),sQuery(id+"F29.wireOp",EDGE,"E82"),sQuery(id+"F29.wireOp",EDGE,"E83")])],"isStart":false});
            var sketch = newSketch(context, id + "F37", { "sketchPlane" : qUnion([Q0])});
            skLineSegment(sketch, "E99", {"start": v(-39.5, 57.45) * mm, "end": v(-20.5, 57.45) * mm, "construction": true});
            skCircle(sketch, "E100", {"center": v(-30, 57.45) * mm, "radius": 1.5 * mm});
            skSolve(sketch);
        }
        {
            var Q0;
            Q0=qSketchRegion(id+"F37",true);
            extrude(context, id + "F38", {"entities" : qUnion([Q0]), "operationType" : NewBodyOperationType.ADD, "depth" : 7 * mm});
        }
        {
            var Q0;
            Q0=makeQuery(id+"F38.opExtrude","CAP_EDGE",EDGE,{"disambiguationData":[OSD([sQuery(id+"F37.wireOp",EDGE,"E100")])],"isStart":false});
            fillet(context, id + "F39", {"entities" : qUnion([Q0]), "radius" : 1.5 * mm, "tangentPropagation" : true, "allowEdgeOverflow" : false});
        }
        {
            var Q0;
            Q0=makeQuery(id+"F36.opExtrude","CAP_FACE",FACE,{"disambiguationData":[OSD([sQuery(id+"F35.wireOp",EDGE,"E98.4.0.0")])],"isStart":false});
            var sketch = newSketch(context, id + "F40", { "sketchPlane" : qUnion([Q0])});
            skCircle(sketch, "E101", {"center": v(42.5, 57.45) * mm, "radius": 1.75 * mm});
            skCircle(sketch, "E102", {"center": v(42.5, 57.45) * mm, "radius": 3 * mm});
            skSolve(sketch);
        }
        {
            var Q0;
            Q0=qSketchRegion(id+"F40",true);
            extrude(context, id + "F41", {"entities" : qUnion([Q0]), "depth" : 0.2 * mm});
        }
        {
            var Q0;
            Q0=makeQuery(id+"F41.opExtrude","CAP_FACE",FACE,{"disambiguationData":[OSD([sQuery(id+"F40.wireOp",EDGE,"E101"),sQuery(id+"F40.wireOp",EDGE,"E102")])],"isStart":false});
            var sketch = newSketch(context, id + "F42", { "sketchPlane" : qUnion([Q0])});
            skCircle(sketch, "E103.0", {"center": v(42.5, 57.45) * mm, "radius": 1.75 * mm});
            skCircle(sketch, "E104", {"center": v(42.5, 57.45) * mm, "radius": 2 * mm});
            skSolve(sketch);
        }
        {
            var Q0;
            Q0=qSketchRegion(id+"F42",true);
            extrude(context, id + "F43", {"entities" : qUnion([Q0]), "operationType" : NewBodyOperationType.ADD, "depth" : 4 * mm});
        }
        {
            var Q0;
            Q0=makeQuery(id+"F43.opExtrude","CAP_FACE",FACE,{"disambiguationData":[OSD([sQuery(id+"F42.wireOp",EDGE,"E103.0"),sQuery(id+"F42.wireOp",EDGE,"E104")])],"isStart":false});
            var sketch = newSketch(context, id + "F44", { "sketchPlane" : qUnion([Q0])});
            skCircle(sketch, "E105.0", {"center": v(42.5, 57.45) * mm, "radius": 2 * mm});
            skSolve(sketch);
        }
        {
            var Q0;
            Q0=qSketchRegion(id+"F44",true);
            extrude(context, id + "F45", {"entities" : qUnion([Q0]), "operationType" : NewBodyOperationType.ADD, "oppositeDirection" : true, "depth" : 3 * mm});
        }
        {
            var Q0;
            {var subQ8=sQuery(id+"F0.wireOp",EDGE,"E0.rect.left");var subQ9=sQuery(id+"F0.wireOp",EDGE,"E0.rect.top");var subQ14=sQuery(id+"F20.wireOp",EDGE,"E68.rect.bottom");var subQ18=sQuery(id+"F12.wireOp",EDGE,"E28.rect.top");var subQ25=sQuery(id+"F16.wireOp",EDGE,"E49.rect.left");var subQ27=sQuery(id+"F16.wireOp",EDGE,"E49.rect.right");var subQ29=sQuery(id+"F16.wireOp",EDGE,"E49.rect.top");var subQ41=makeQuery(id+"F1.opExtrude","SWEPT_FACE",FACE,{"disambiguationData":[OSD([subQ8])]});var subQ53=sQuery(id+"F12.wireOp",EDGE,"E28.rect.left");var subQ56=sQuery(id+"F12.wireOp",EDGE,"E28.rect.right");var subQ70=sQuery(id+"F20.wireOp",EDGE,"E69.rect.bottom");Q0=makeQuery(id+"F23.boolean.opBoolean","SPLIT",FACE,{"disambiguationData":[TD([subQ41])],"derivedFrom":makeQuery(id+"F21.boolean.opBoolean","MERGE",FACE,{"derivedFrom":[makeQuery(id+"F19.boolean.opBoolean","SPLIT",FACE,{"disambiguationData":[TD([subQ41])],"derivedFrom":makeQuery(id+"F17.boolean.opBoolean","MERGE",FACE,{"derivedFrom":[makeQuery(id+"F15.boolean.opBoolean","SPLIT",FACE,{"disambiguationData":[TD([subQ41])],"derivedFrom":makeQuery(id+"F13.boolean.opBoolean","MERGE",FACE,{"derivedFrom":[makeQuery(id+"F1.opExtrude","SWEPT_FACE",FACE,{"disambiguationData":[OSD([subQ9])]}),makeQuery(id+"F13.opExtrude","CAP_FACE",FACE,{"disambiguationData":[OSD([sQuery(id+"F12.wireOp",EDGE,"E28.rect.bottom"),subQ18,subQ53,subQ56])],"isStart":true})]})}),makeQuery(id+"F17.opExtrude","CAP_FACE",FACE,{"disambiguationData":[OSD([sQuery(id+"F16.wireOp",EDGE,"E49.rect.bottom"),subQ29,subQ25,subQ27])],"isStart":true})]})}),makeQuery(id+"F21.opExtrude","SWEPT_FACE",FACE,{"disambiguationData":[OSD([subQ14])]}),makeQuery(id+"F21.opExtrude","SWEPT_FACE",FACE,{"disambiguationData":[OSD([subQ70])]})]})});}
            var sketch = newSketch(context, id + "F46", { "sketchPlane" : qUnion([Q0])});
            skLineSegment(sketch, "E106.bottom", {"start": v(-29.75, 10.8) * mm, "end": v(7.75, 10.8) * mm});
            skLineSegment(sketch, "E106.top", {"start": v(-29.75, 0) * mm, "end": v(7.75, 0) * mm});
            skLineSegment(sketch, "E106.left", {"start": v(-29.75, 10.8) * mm, "end": v(-29.75, 0) * mm});
            skLineSegment(sketch, "E106.right", {"start": v(7.75, 10.8) * mm, "end": v(7.75, 0) * mm});
            skLineSegment(sketch, "E107.bottom", {"start": v(42, 0) * mm, "end": v(11, 0) * mm});
            skLineSegment(sketch, "E107.top", {"start": v(42, 12) * mm, "end": v(11, 12) * mm});
            skLineSegment(sketch, "E107.left", {"start": v(42, 0) * mm, "end": v(42, 12) * mm});
            skLineSegment(sketch, "E107.right", {"start": v(11, 0) * mm, "end": v(11, 12) * mm});
            skSolve(sketch);
        }
        {
            var Q0;
            Q0 = qSketchRegion(id + "F46", true);
            var Q1;
            Q1=makeQuery(id+"F15.opExtrude","CAP_FACE",FACE,{"disambiguationData":[OSD([sQuery(id+"F14.wireOp",EDGE,"E30"),sQuery(id+"F14.wireOp",EDGE,"E31"),sQuery(id+"F14.wireOp",EDGE,"E32"),sQuery(id+"F14.wireOp",EDGE,"E33"),sQuery(id+"F14.wireOp",EDGE,"E34.MirrorCS"),sQuery(id+"F14.wireOp",EDGE,"E35.MirrorCS"),sQuery(id+"F14.wireOp",EDGE,"E36.MirrorCS"),sQuery(id+"F14.wireOp",EDGE,"E37.MirrorCS")])],"isStart":false});
            extrude(context, id + "F47", {"entities" : qUnion([Q0]), "operationType" : NewBodyOperationType.ADD, "endBound" : BoundingType.UP_TO_SURFACE, "endBoundEntityFace" : qUnion([Q1]), "depth" : 25 * mm});
        }
    });
